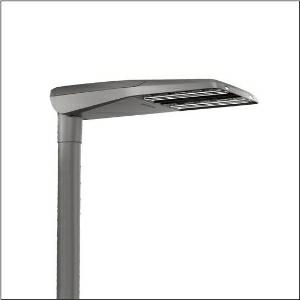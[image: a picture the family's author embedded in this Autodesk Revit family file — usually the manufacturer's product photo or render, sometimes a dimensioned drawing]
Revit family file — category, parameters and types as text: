
# Revit family: streetlight_sl_11_iq_midi___st1_2p1_0_5xc3g51e08me_ff57
name_source: partatom
category: Lighting Fixtures
units: mm (PartAtom-declared; Revit-internal decimal feet)

## family parameters
Cut with Voids When Loaded = No
Host = Face
Light Source = No
Part Type = Normal
Room Calculation Point = No
Round Connector Dimension = Use Diameter
Shared = No

## types (1)
- --- (1 x LED, 17750 lm, 121.7 W, 3000K)
    Apparent Load = 122 VA
    CIE Flux Codes = 31 68 95 100 100
    Color Rendering = 70
    Color Temperature = 3000K
    Default Elevation = 1800 mm
    Description = Streetlight SL 11 iQ midi, mast luminaire, primary light control with 3 zone facetted reflector, of plastic, silver coated, highly specular, primary optical cover: cover, of PMMA, transparent, light distribution: ST1.2P1.0, light emission: direct distribution, primary light characteristic: asymmetric, installation type: post-top, side-entry, lamps: LED, High Power LED, rated values: 17.750lm | 121,7W | 145,9lm/W (begin service life); end service life: 17.750lm | 129W; at 50% lumin. flux: 8.875lm | 56W | 158,5lm/W, colour temperature: 3000K, colour rendering: CRI > 70, light colour: 730, light setting 1 begin service life: 100% | 17.750lm | 121,7W | 145,9lm/W | 3.000K, light setting 1 end service life: 129W, further light settings possible, control: optimised constant luminous flux control (CLO 2.0), Desk-Remote (wireless, voltage-free reading and setting of iQ features in the workshop via application-optimized NFC function/RFID function), Light-Fading, Smart-Wire, Night-Set, Lumen-Switch, Temp-Guard, Auto-Match, with cable H07RN-F 5x 1.5mm², mains connection: 230..240V, AC, 50/60Hz, connection cable pre-assembled, cable length: 12,5m, luminaire housing, of diecast aluminium, powder-coated, Siteco® metallic grey (DB 702S), please order mast flange separately, inclination adjustable without tools: 0°, 5°, 10°, 15° (post-top) | 0°, -5°, -10°, -15° (side-entry), sealing non-destructively replaceable, multi-level sealing system, length: 780mm, width: 376mm, height: 118mm, mast flange for spigot size: 42mm (side-entry): 5XC10008XM4, 60/48mm (side-entry/post-top): 5XC10108XM2, 76/60mm (side-entry/post-top): 5XC10108XM1, equipment: Power, protection rating (complete): IP66, insulation class (complete): insulation class II (safety insulation), certification: CE, ENEC, ENEC+, VDE, impact resistance: IK10, permissible operating ambient temperature for outdoor applications: -25..+50°C, standard-compliant lighting for roads and squares, Environmental Product Declaration (EPD) tested and certified by an independent institute, packaging unit: 1 piece

Light Distribution: ST1.2P1.0
    Height = 118 mm
    Lamp = 1 x LED
    Lamp Light Flux = 17750 lm
    Lamp Power = 121.7 W
    Lamp count = 1
    Length = 780 mm
    Luminous efficacy = 146 lm/W
    Manufacturer = Siteco
    ModVariant = No
    Model = 5XC3G51E08ME
    Number of Poles = 1
    OnlyDefault = Yes
    Power Factor = 1
    Product Name = Streetlight SL 11 iQ midi | ST1.2P1.0
    Product group = mast luminaire | pylon top
    ProductGroupID = 6100
    Protection Class = Protection class II
    Protection Degree = IP 66
    RLX_Detail_Level = 1
    RLX_Emergency_Light_Flux = 0 lm
    RLX_Emergency_Type = 0
    RLX_Emergency_Type_DB = No
    RlxData = <blob elided: 70845 chars, md5=7714b8b4>
    Socket = socket
    Standby Power = 0 W
    System Light Flux = 17750 lm
    System Power = 122 W
    Type Comments = factory setting: luminous flux: 100 % | dim-lin: 254 | 544 mA
    Type Image = l_1005960.jpg
    URL = http://relux.com
    VarID = @adj_057567
    Voltage = 0 V
    Weight = 0.00 kg
    Width = 376 mm

## geometry (parser evidence)
native form markers: Blend x4, Sweep x8
no freeform markers — native parametric forms only
